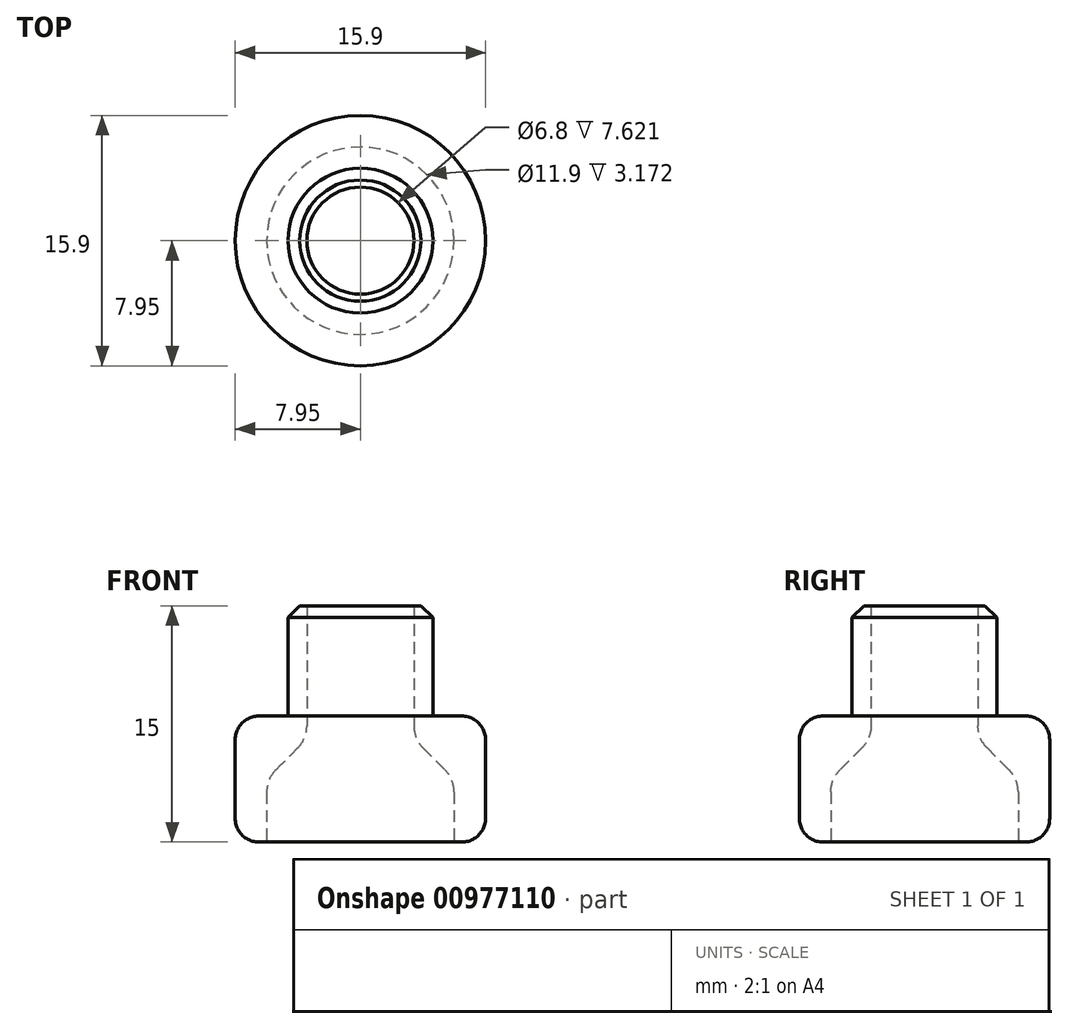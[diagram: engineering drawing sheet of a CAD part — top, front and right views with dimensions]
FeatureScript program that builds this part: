
annotation { "Feature Type Name" : "Feature", "Feature Type Description" : "" }
export const myFeature = defineFeature(function(context is Context, id is Id, definition is map)
    precondition{}
    {
        {
            var Q0;
            Q0=qCreatedBy(makeId("Front.planeOp"),FACE);
            var sketch = newSketch(context, id + "F0", { "sketchPlane" : qUnion([Q0])});
            skLineSegment(sketch, "E0", {"start": v(-7.95, 0) * mm, "end": v(7.95, 0) * mm});
            skLineSegment(sketch, "E1", {"start": v(0, 0) * mm, "end": v(0, 69.21) * mm});
            skLineSegment(sketch, "E2", {"start": v(-4.6, 8) * mm, "end": v(4.6, 8) * mm});
            skPoint(sketch, "E3", {"position": v(0, 8) * mm});
            skLineSegment(sketch, "E4.0", {"start": v(-7.95, 8) * mm, "end": v(7.95, 8) * mm});
            skLineSegment(sketch, "E5.0", {"start": v(-4.6, 15) * mm, "end": v(4.6, 15) * mm});
            skLineSegment(sketch, "E6", {"start": v(4.6, 15) * mm, "end": v(4.6, 8) * mm});
            skLineSegment(sketch, "E7", {"start": v(7.95, 8) * mm, "end": v(7.95, 0) * mm});
            skLineSegment(sketch, "E8.0", {"start": v(5.95, 8) * mm, "end": v(5.95, 0) * mm});
            skLineSegment(sketch, "E9.0", {"start": v(3.4, 15) * mm, "end": v(3.4, 8.05) * mm});
            skLineSegment(sketch, "E10", {"start": v(3.4, 8.05) * mm, "end": v(3.4, 6.55) * mm});
            skLineSegment(sketch, "E11", {"start": v(3.4, 6.55) * mm, "end": v(5.95, 4) * mm});
            skSolve(sketch);
        }
        {
            var Q0;
            {var subQ1=sQuery(id+"F0.wireOp",EDGE,"E6");Q0=makeQuery(id+"F0.imprint","IMPRINT",FACE,{"disambiguationData":[TD([[makeQuery(id+"F0.imprint","IMPRINT",EDGE,{"derivedFrom":subQ1}),-1.0]])]});}
            var Q1;
            {var subQ3=sQuery(id+"F0.wireOp",EDGE,"E11");Q1=makeQuery(id+"F0.imprint","IMPRINT",FACE,{"disambiguationData":[TD([[makeQuery(id+"F0.imprint","IMPRINT",EDGE,{"derivedFrom":subQ3}),1.0]])]});}
            var Q2;
            {var subQ4=sQuery(id+"F0.wireOp",EDGE,"E7");Q2=makeQuery(id+"F0.imprint","IMPRINT",FACE,{"disambiguationData":[TD([[makeQuery(id+"F0.imprint","IMPRINT",EDGE,{"derivedFrom":subQ4}),-1.0]])]});}
            var Q3;
            Q3=sQuery(id+"F0.wireOp",EDGE,"E1");
            revolve(context, id + "F1", {"surfaceOperationType" : NewSurfaceOperationType.NEW, "entities" : qUnion([Q0, Q1, Q2]), "axis" : qUnion([Q3]), "revolveType" : RevolveType.FULL});
        }
        {
            var Q0;
            Q0=makeQuery(id+"F1.opRevolve","SWEPT_EDGE",EDGE,{"disambiguationData":[OSD([sQuery(id+"F0.wireOp",EDGE,"E4.0"),sQuery(id+"F0.wireOp",EDGE,"E7")])]});
            var Q1;
            Q1=makeQuery(id+"F1.opRevolve","SWEPT_EDGE",EDGE,{"disambiguationData":[OSD([sQuery(id+"F0.wireOp",EDGE,"E0"),sQuery(id+"F0.wireOp",EDGE,"E7")])]});
            fillet(context, id + "F2", {"entities" : qUnion([Q0, Q1]), "radius" : 1.5 * mm, "tangentPropagation" : true, "allowEdgeOverflow" : false});
        }
        {
            var Q0;
            Q0=makeQuery(id+"F1.opRevolve","SWEPT_EDGE",EDGE,{"disambiguationData":[OSD([sQuery(id+"F0.wireOp",EDGE,"E5.0"),sQuery(id+"F0.wireOp",EDGE,"E6")])]});
            chamfer(context, id + "F3", {"entities" : qUnion([Q0]), "width" : .75 * mm, "tangentPropagation" : true});
        }
        {
            var Q0;
            Q0=makeQuery(id+"F1.opRevolve","SWEPT_EDGE",EDGE,{"disambiguationData":[OSD([sQuery(id+"F0.wireOp",EDGE,"E10"),sQuery(id+"F0.wireOp",EDGE,"E11")])]});
            var Q1;
            Q1=makeQuery(id+"F1.opRevolve","SWEPT_EDGE",EDGE,{"disambiguationData":[OSD([sQuery(id+"F0.wireOp",EDGE,"E8.0"),sQuery(id+"F0.wireOp",EDGE,"E11")])]});
            fillet(context, id + "F4", {"entities" : qUnion([Q0, Q1]), "radius" : 2 * mm, "tangentPropagation" : true, "allowEdgeOverflow" : false});
        }
    });
